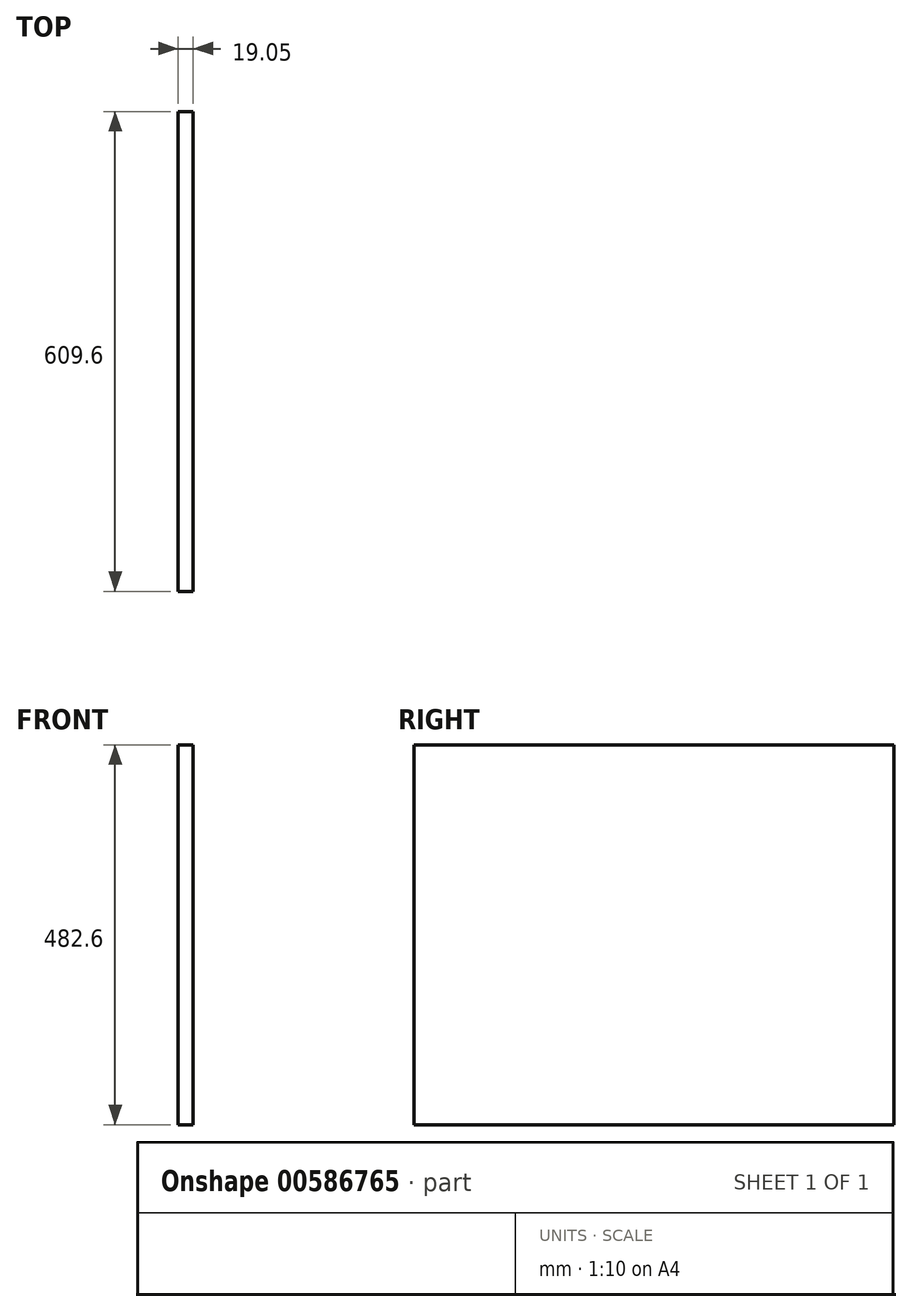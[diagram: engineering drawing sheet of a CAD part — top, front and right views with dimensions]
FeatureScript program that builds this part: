
annotation { "Feature Type Name" : "Feature", "Feature Type Description" : "" }
export const myFeature = defineFeature(function(context is Context, id is Id, definition is map)
    precondition{}
    {
        {
            var Q0;
            Q0=qCreatedBy(makeId("Right.planeOp"),FACE);
            var sketch = newSketch(context, id + "F0", { "sketchPlane" : qUnion([Q0])});
            skLineSegment(sketch, "E0.bottom", {"start": v(-296.65, 244.65) * mm, "end": v(312.95, 244.65) * mm});
            skLineSegment(sketch, "E0.top", {"start": v(-296.65, -237.95) * mm, "end": v(312.95, -237.95) * mm});
            skLineSegment(sketch, "E0.left", {"start": v(-296.65, 244.65) * mm, "end": v(-296.65, -237.95) * mm});
            skLineSegment(sketch, "E0.right", {"start": v(312.95, 244.65) * mm, "end": v(312.95, -237.95) * mm});
            skSolve(sketch);
        }
        {
            var Q0;
            Q0 = qSketchRegion(id + "F0", true);
            extrude(context, id + "F1", {"entities" : qUnion([Q0]), "depth" : 19.05 * mm, "offsetDistance" : 25.4 * mm});
        }
    });
